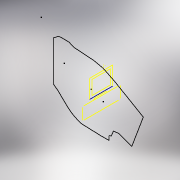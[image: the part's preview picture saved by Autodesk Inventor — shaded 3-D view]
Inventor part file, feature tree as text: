
AUTODESK INVENTOR PART (.ipt)
format: ipt  version: 2022 (Build 260153000, 153)  size: 115,712 bytes
history: native  units: mm
features: reference x15, sketch x3, other x3
ambient origin geometry x8: Origin, YZ Plane, XZ Plane, XY Plane, X Axis, Y Axis, Z Axis, Center Point
feature tree (21):
  sketch  "Sketch1"
  sketch  "Sketch2"
  sketch  "Sketch3"
  reference  "Reference25"
  reference  "Reference26"
  reference  "Reference27"
  reference  "Reference28"
  reference  "Reference29"
  reference  "Reference30"
  reference  "Reference31"
  reference  "Reference32"
  reference  "Reference33"
  reference  "Reference34"
  reference  "Reference35"
  reference  "Reference36"
  reference  "Reference37"
  reference  "Reference38"
  reference  "Reference39"
  other  "<userpath>\Desktop\fun\Chappy.iam"
  other  "Chappy.iam"
  other  "NEW:1"
